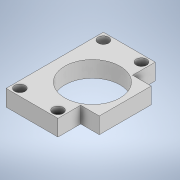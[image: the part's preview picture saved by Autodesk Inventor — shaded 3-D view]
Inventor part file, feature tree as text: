
AUTODESK INVENTOR PART (.ipt)
format: ipt  version: 2020.1 (Build 241239000, 239)  size: 130,560 bytes
history: native  units: mm
features: other x1, extrude x1, sketch x1
ambient origin geometry x8: Origin, YZ Plane, XZ Plane, XY Plane, X Axis, Y Axis, Z Axis, Center Point
bodies: Body1 (feature_tree)
feature tree (3):
  other  "Твердое тело1"
  extrude  "Выдавливание1"  Depth=10.0mm TaperAngle=0.0deg
  sketch  "Эскиз1"
